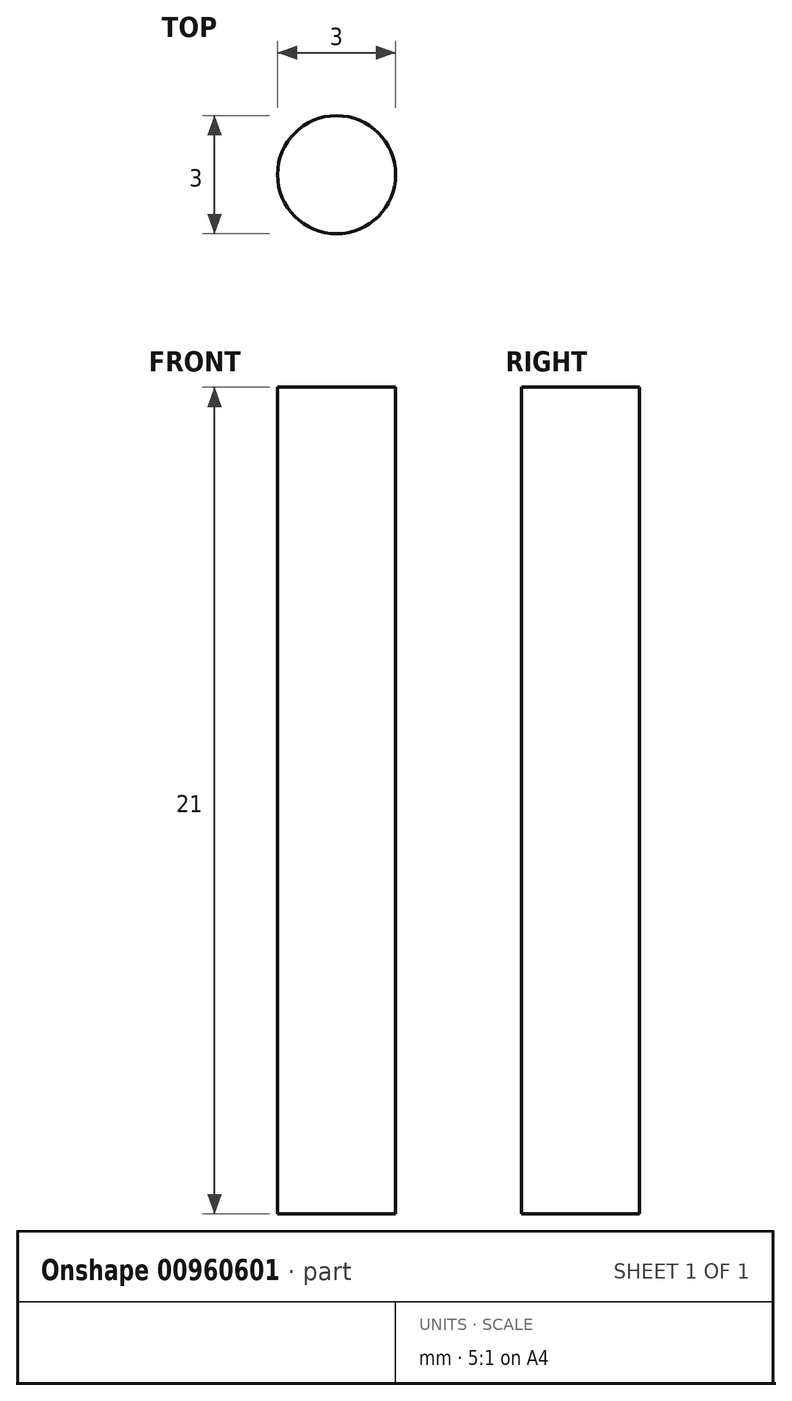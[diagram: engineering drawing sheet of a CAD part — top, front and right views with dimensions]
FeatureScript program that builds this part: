
annotation { "Feature Type Name" : "Feature", "Feature Type Description" : "" }
export const myFeature = defineFeature(function(context is Context, id is Id, definition is map)
    precondition{}
    {
        {
            var Q0;
            Q0=qCreatedBy(makeId("Top.planeOp"),FACE);
            var sketch = newSketch(context, id + "F0", { "sketchPlane" : qUnion([Q0])});
            skCircle(sketch, "E0", {"center": v(0, 0) * mm, "radius": 1.5 * mm});
            skSolve(sketch);
        }
        {
            var Q0;
            Q0=makeQuery(id+"F0.imprint","IMPRINT",FACE,{"disambiguationData":[TD([[makeQuery(id+"F0.imprint","IMPRINT",EDGE,{"derivedFrom":sQuery(id+"F0.wireOp",EDGE,"E0")}),1.0]])]});
            extrude(context, id + "F1", {"entities" : qUnion([Q0]), "depth" : 21 * mm, "offsetDistance" : 25 * mm});
        }
    });
